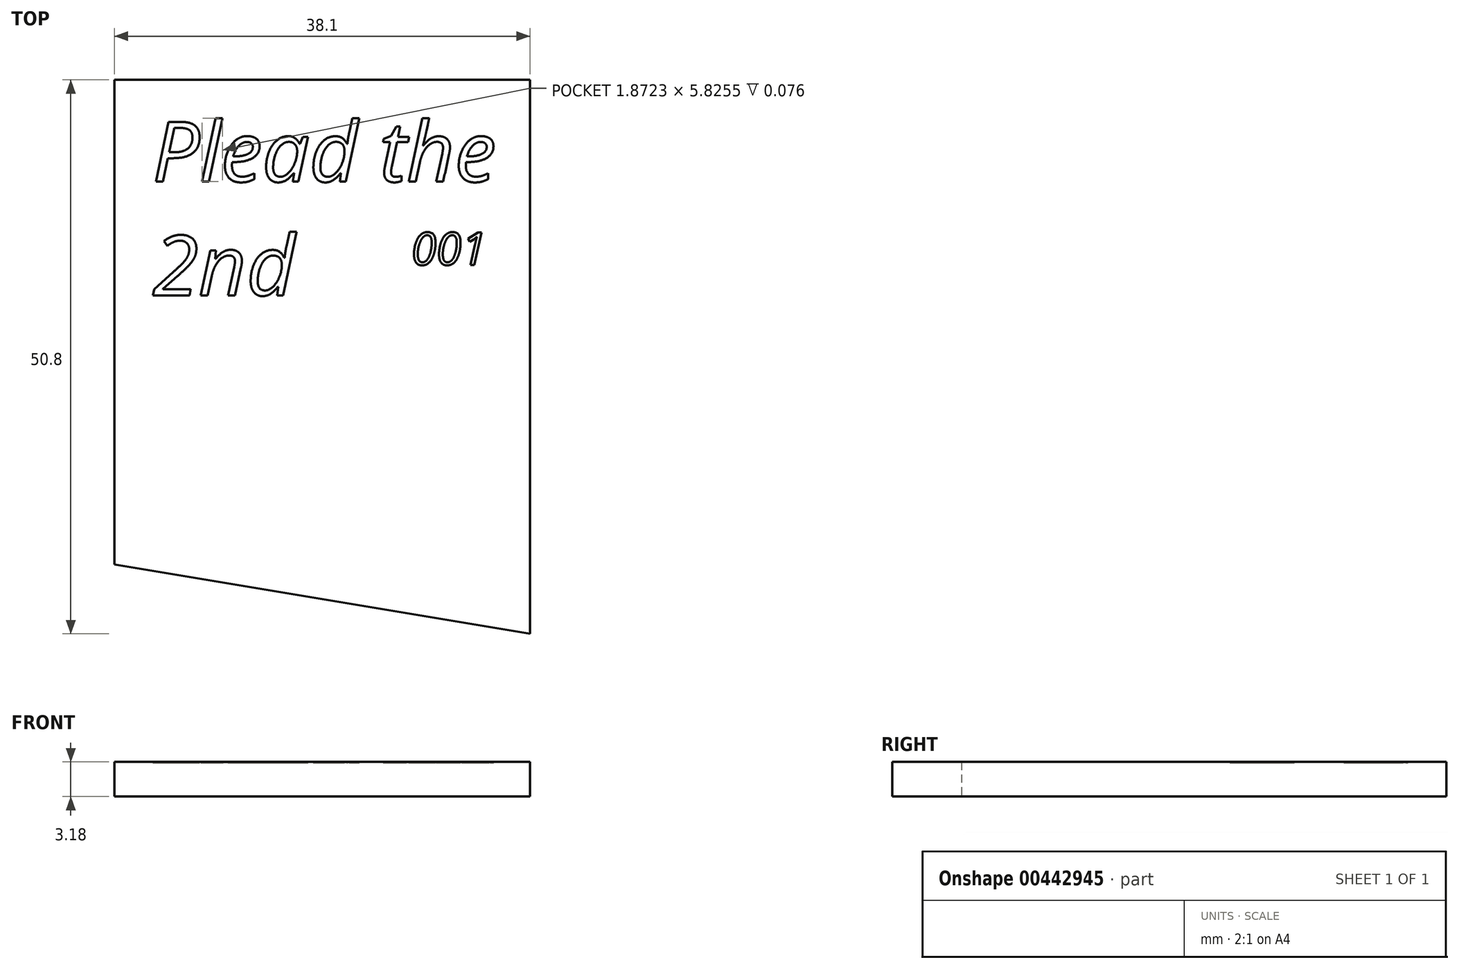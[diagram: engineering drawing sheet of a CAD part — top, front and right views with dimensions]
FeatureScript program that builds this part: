
annotation { "Feature Type Name" : "Feature", "Feature Type Description" : "" }
export const myFeature = defineFeature(function(context is Context, id is Id, definition is map)
    precondition{}
    {
        {
            var Q0;
            Q0=qCreatedBy(makeId("Top.planeOp"),FACE);
            var sketch = newSketch(context, id + "F0", { "sketchPlane" : qUnion([Q0])});
            skLineSegment(sketch, "E0.bottom", {"start": v(-19.05, 25.4) * mm, "end": v(19.05, 25.4) * mm});
            skLineSegment(sketch, "E0.right", {"start": v(19.05, 25.4) * mm, "end": v(19.05, -25.4) * mm});
            skPoint(sketch, "E0.middle", {"position": v(0, 0) * mm});
            skLineSegment(sketch, "E1", {"start": v(-19.05, 25.4) * mm, "end": v(-19.05, -19.05) * mm});
            skLineSegment(sketch, "E2", {"start": v(-19.05, -19.05) * mm, "end": v(19.05, -25.4) * mm});
            skSolve(sketch);
        }
        {
            var Q0;
            Q0=qSketchRegion(id+"F0",true);
            extrude(context, id + "F1", {"entities" : qUnion([Q0]), "depth" : 3.17 * mm});
        }
        {
            var Q0;
            Q0=makeQuery(id+"F1.opExtrude","CAP_FACE",FACE,{"disambiguationData":[OSD([sQuery(id+"F0.wireOp",EDGE,"E0.bottom"),sQuery(id+"F0.wireOp",EDGE,"E0.right"),sQuery(id+"F0.wireOp",EDGE,"E1"),sQuery(id+"F0.wireOp",EDGE,"E2")])],"isStart":false});
            var sketch = newSketch(context, id + "F2", { "sketchPlane" : qUnion([Q0])});
            skText(sketch, "E3", { "text": "Plead the\n2nd", "fontName": "OpenSans-Italic.ttf"});
            const initialGuessF2  = {"E3": [-0.01557, 0.01606, 1, 0, 0.00552]};
            skSetInitialGuess(sketch, initialGuessF2);
            skSolve(sketch);
        }
        {
            var Q0;
            Q0=qSketchRegion(id+"F2",true);
            extrude(context, id + "F3", {"entities" : qUnion([Q0]), "operationType" : NewBodyOperationType.REMOVE, "oppositeDirection" : true, "depth" : 0.08 * mm});
        }
        {
            var Q0;
            {var subQ0=sQuery(id+"F0.wireOp",EDGE,"E0.right");var subQ1=sQuery(id+"F0.wireOp",EDGE,"E2");var subQ2=sQuery(id+"F0.wireOp",EDGE,"E0.bottom");var subQ3=sQuery(id+"F0.wireOp",EDGE,"E1");Q0=makeQuery(id+"F3.boolean.opBoolean","SPLIT",FACE,{"disambiguationData":[TD([makeQuery(id+"F1.opExtrude","SWEPT_FACE",FACE,{"disambiguationData":[OSD([subQ2])]})])],"derivedFrom":makeQuery(id+"F1.opExtrude","CAP_FACE",FACE,{"disambiguationData":[OSD([subQ2,subQ0,subQ3,subQ1])],"isStart":false})});}
            var sketch = newSketch(context, id + "F4", { "sketchPlane" : qUnion([Q0])});
            skText(sketch, "E4", { "text": "001", "fontName": "OpenSans-Italic.ttf"});
            const initialGuessF4  = {"E4": [0.00817, 0.00842, 1, 0, 0.003]};
            skSetInitialGuess(sketch, initialGuessF4);
            skSolve(sketch);
        }
        {
            var Q0;
            Q0=qSketchRegion(id+"F4",true);
            extrude(context, id + "F5", {"entities" : qUnion([Q0]), "operationType" : NewBodyOperationType.REMOVE, "oppositeDirection" : true, "depth" : 0.08 * mm});
        }
    });
